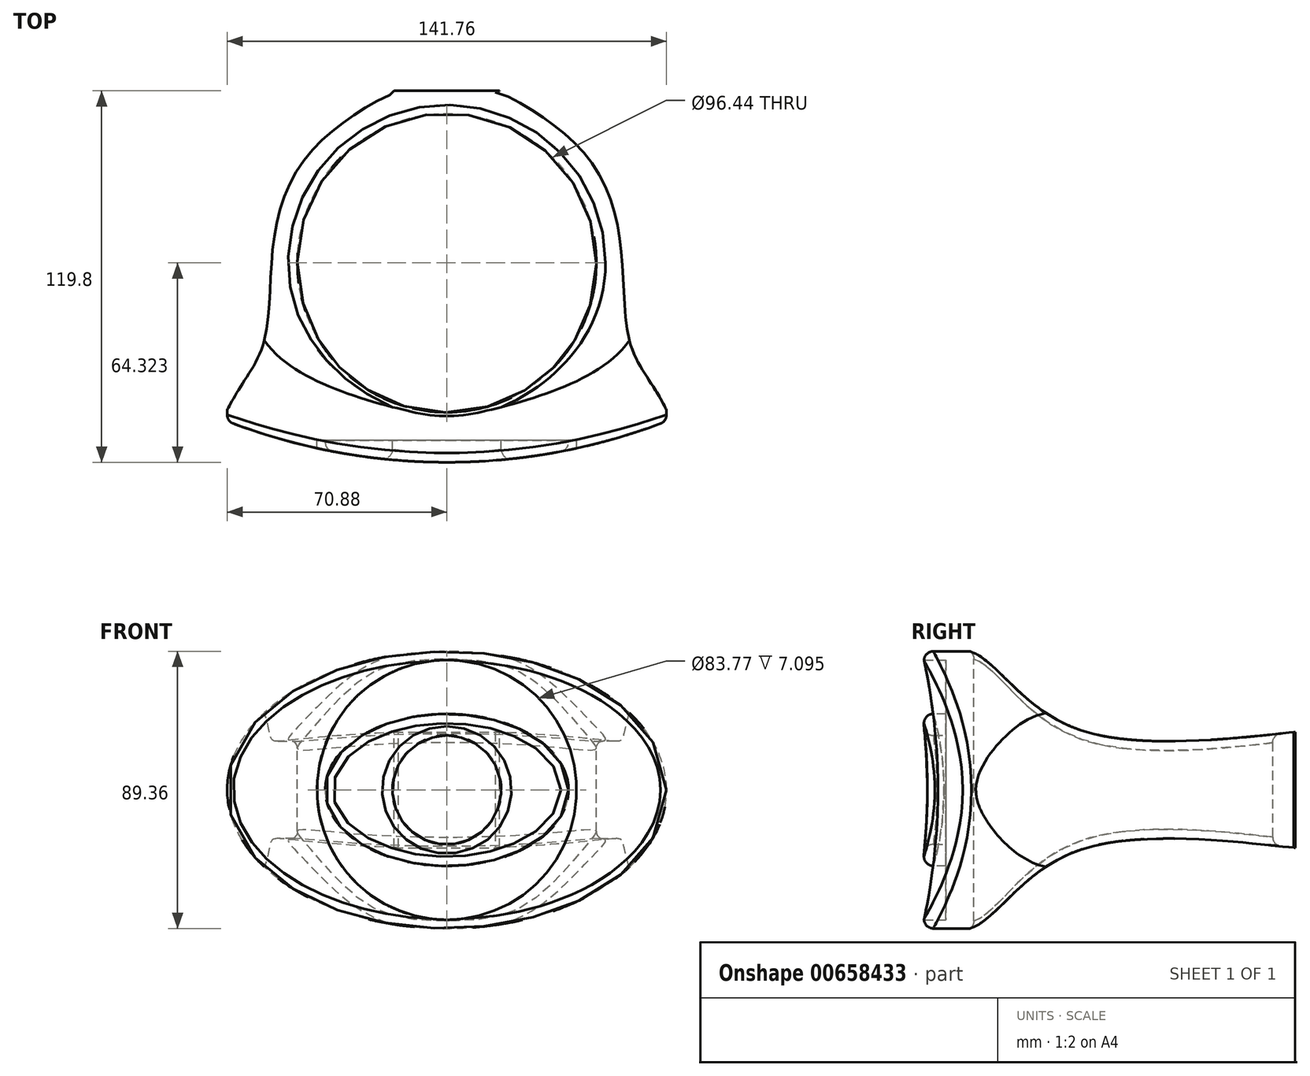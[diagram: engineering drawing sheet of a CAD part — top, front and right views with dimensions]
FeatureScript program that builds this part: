
annotation { "Feature Type Name" : "Feature", "Feature Type Description" : "" }
export const myFeature = defineFeature(function(context is Context, id is Id, definition is map)
    precondition{}
    {
        {
            var Q0;
            Q0=qCreatedBy(makeId("Front.planeOp"),FACE);
            var sketch = newSketch(context, id + "F0", { "sketchPlane" : qUnion([Q0])});
            skCircle(sketch, "E0", {"center": v(0, 0) * mm, "radius": 17.57 * mm});
            skCircle(sketch, "E1", {"center": v(0, 0) * mm, "radius": 41.88 * mm});
            skEllipse(sketch, "E2", {"center": v(0, 0) * mm, "majorRadius": 39.25 * mm, "minorRadius": 24.52 * mm, "majorAxis": v(1, 0)});
            skEllipse(sketch, "E3", {"center": v(0, 0) * mm, "majorRadius": 70.88 * mm, "minorRadius": 44.68 * mm, "majorAxis": v(1, 0)});
            skSolve(sketch);
        }
        {
            var Q0;
            Q0=makeQuery(id+"F0.imprint","IMPRINT",FACE,{"disambiguationData":[TD([[makeQuery(id+"F0.imprint","IMPRINT",EDGE,{"derivedFrom":sQuery(id+"F0.wireOp",EDGE,"E0")}),-1.0]])]});
            var Q1;
            Q1=makeQuery(id+"F0.imprint","IMPRINT",FACE,{"disambiguationData":[TD([[makeQuery(id+"F0.imprint","IMPRINT",EDGE,{"derivedFrom":sQuery(id+"F0.wireOp",EDGE,"E1")}),-1.0]])]});
            extrude(context, id + "F1", {"entities" : qUnion([Q0, Q1]), "depth" : 25.4 * mm, "offsetDistance" : 25.4 * mm});
        }
        {
            var Q0;
            Q0=qCreatedBy(makeId("Top.planeOp"),FACE);
            var sketch = newSketch(context, id + "F2", { "sketchPlane" : qUnion([Q0])});
            skCircle(sketch, "E4", {"center": v(0, 182.47) * mm, "radius": 196.57 * mm});
            skCircle(sketch, "E5", {"center": v(0, 182.47) * mm, "radius": 224.82 * mm});
            skSolve(sketch);
        }
        {
            var Q0;
            Q0=makeQuery(id+"F2.imprint","IMPRINT",FACE,{"disambiguationData":[TD([[makeQuery(id+"F2.imprint","IMPRINT",EDGE,{"derivedFrom":sQuery(id+"F2.wireOp",EDGE,"E4")}),-1.0]])]});
            extrude(context, id + "F3", {"entities" : qUnion([Q0]), "endBound" : BoundingType.SYMMETRIC, "depth" : 127 * mm, "offsetDistance" : 25.4 * mm});
        }
        {
            var Q0;
            Q0=makeQuery(id+"F3.opExtrude","SWEPT_BODY",BODY,{"disambiguationData":[OSD([sQuery(id+"F2.wireOp",EDGE,"E4"),sQuery(id+"F2.wireOp",EDGE,"E5")])]});
            var Q1;
            Q1=makeQuery(id+"F1.opExtrude","SWEPT_BODY",BODY,{"disambiguationData":[OSD([sQuery(id+"F0.wireOp",EDGE,"E1"),sQuery(id+"F0.wireOp",EDGE,"E3")])]});
            var Q2;
            Q2=makeQuery(id+"F1.opExtrude","SWEPT_BODY",BODY,{"disambiguationData":[OSD([sQuery(id+"F0.wireOp",EDGE,"E0"),sQuery(id+"F0.wireOp",EDGE,"E2")])]});
            booleanBodies(context, id + "F4", {"operationType" : BooleanOperationType.SUBTRACTION, "tools" : qUnion([Q0]), "targets" : qUnion([Q1, Q2])});
        }
        {
            var Q0;
            Q0=makeQuery(id+"F1.opExtrude","CAP_FACE",FACE,{"disambiguationData":[OSD([sQuery(id+"F0.wireOp",EDGE,"E1"),sQuery(id+"F0.wireOp",EDGE,"E3")])],"isStart":true});
            var sketch = newSketch(context, id + "F5", { "sketchPlane" : qUnion([Q0])});
            skEllipse(sketch, "E6", {"center": v(0, 0) * mm, "majorRadius": 70.88 * mm, "minorRadius": 44.68 * mm, "majorAxis": v(1, 0)});
            skSolve(sketch);
        }
        {
            var Q0;
            Q0 = qSketchRegion(id + "F5", true);
            extrude(context, id + "F6", {"entities" : qUnion([Q0]), "depth" : 105.7 * mm, "offsetDistance" : 25 * mm});
        }
        {
            var Q0;
            Q0=makeQuery(id+"F1.opExtrude","SWEPT_BODY",BODY,{"disambiguationData":[OSD([sQuery(id+"F0.wireOp",EDGE,"E0"),sQuery(id+"F0.wireOp",EDGE,"E2")])]});
            var Q1;
            Q1=makeQuery(id+"F1.opExtrude","SWEPT_BODY",BODY,{"disambiguationData":[OSD([sQuery(id+"F0.wireOp",EDGE,"E1"),sQuery(id+"F0.wireOp",EDGE,"E3")])]});
            var Q2;
            Q2=makeQuery(id+"F6.opExtrude","SWEPT_BODY",BODY,{"disambiguationData":[OSD([sQuery(id+"F5.wireOp",EDGE,"E6")])]});
            booleanBodies(context, id + "F7", {"operationType" : BooleanOperationType.UNION, "tools" : qUnion([Q0, Q1, Q2])});
        }
        {
            var Q0;
            Q0=qCreatedBy(makeId("Top.planeOp"),FACE);
            var sketch = newSketch(context, id + "F8", { "sketchPlane" : qUnion([Q0])});
            skCircle(sketch, "E7", {"center": v(0, 50.22) * mm, "radius": 48.22 * mm});
            skSolve(sketch);
        }
        {
            var Q0;
            Q0 = qSketchRegion(id + "F8", true);
            extrude(context, id + "F9", {"entities" : qUnion([Q0]), "operationType" : NewBodyOperationType.REMOVE, "endBound" : BoundingType.SYMMETRIC, "oppositeDirection" : true, "depth" : 100 * mm, "offsetDistance" : 25 * mm});
        }
        {
            var Q0;
            Q0=qCreatedBy(makeId("Top.planeOp"),FACE);
            var sketch = newSketch(context, id + "F10", { "sketchPlane" : qUnion([Q0])});
            skFitSpline(sketch, "E8", {"points": [v(-73.16, -11.53) * mm, v(-72.85, -3.9) * mm, v(-66.49, 10.46) * mm, v(-58.83, 25.54) * mm, v(-55.73, 58.48) * mm, v(-40.14, 89.97) * mm, v(-15.99, 105.25) * mm, v(-15.68, 105.25) * mm, v(-89.05, 104.33) * mm, v(-82.63, -12.15) * mm, v(-73.16, -11.53) * mm]});
            skFitSpline(sketch, "E9.MirrorC", {"points": [v(73.16, -11.53) * mm, v(72.85, -3.9) * mm, v(66.49, 10.46) * mm, v(58.83, 25.54) * mm, v(55.73, 58.48) * mm, v(40.14, 89.97) * mm, v(15.99, 105.25) * mm, v(15.68, 105.25) * mm, v(89.05, 104.33) * mm, v(82.63, -12.15) * mm, v(73.16, -11.53) * mm]});
            skSolve(sketch);
        }
        {
            var Q0;
            Q0 = qSketchRegion(id + "F10", true);
            extrude(context, id + "F11", {"entities" : qUnion([Q0]), "operationType" : NewBodyOperationType.REMOVE, "endBound" : BoundingType.SYMMETRIC, "oppositeDirection" : true, "depth" : 100 * mm, "offsetDistance" : 25 * mm});
        }
        {
            var Q0;
            Q0=qCreatedBy(makeId("Right.planeOp"),FACE);
            var sketch = newSketch(context, id + "F12", { "sketchPlane" : qUnion([Q0])});
            skFitSpline(sketch, "E10", {"points": [v(-21.85, 47.3) * mm, v(-14.13, 45.68) * mm, v(2.08, 44.23) * mm, v(38.16, 18.74) * mm, v(109.17, 18.74) * mm, v(109.96, 18.74) * mm, v(110.22, 55.95) * mm, v(-24.73, 63.03) * mm, v(-21.85, 47.3) * mm]});
            skFitSpline(sketch, "E11.MirrorC", {"points": [v(-21.85, -47.3) * mm, v(-14.13, -45.68) * mm, v(2.08, -44.23) * mm, v(38.16, -18.74) * mm, v(109.17, -18.74) * mm, v(109.96, -18.74) * mm, v(110.22, -55.95) * mm, v(-24.73, -63.03) * mm, v(-21.85, -47.3) * mm]});
            skSolve(sketch);
        }
        {
            var Q0;
            Q0=makeQuery(id+"F12.imprint","IMPRINT",FACE,{"disambiguationData":[TD([[makeQuery(id+"F12.imprint","IMPRINT",EDGE,{"derivedFrom":sQuery(id+"F12.wireOp",EDGE,"E10")}),1.0]])]});
            var Q1;
            Q1=makeQuery(id+"F12.imprint","IMPRINT",FACE,{"disambiguationData":[TD([[makeQuery(id+"F12.imprint","IMPRINT",EDGE,{"derivedFrom":sQuery(id+"F12.wireOp",EDGE,"E11.MirrorC")}),-1.0]])]});
            extrude(context, id + "F13", {"entities" : qUnion([Q0, Q1]), "operationType" : NewBodyOperationType.REMOVE, "endBound" : BoundingType.SYMMETRIC, "oppositeDirection" : true, "depth" : 150 * mm, "offsetDistance" : 25 * mm});
        }
        {
            var Q0;
            Q0=makeQuery(id+"F13.boolean.opBoolean","INTERSECT",EDGE,{"derivedFrom":[makeQuery(id+"F9.boolean.opBoolean","COPY",FACE,{"derivedFrom":makeQuery(id+"F9.opExtrude","SWEPT_FACE",FACE,{"disambiguationData":[OSD([sQuery(id+"F8.wireOp",EDGE,"E7")])]})}),makeQuery(id+"F13.opExtrude","SWEPT_FACE",FACE,{"disambiguationData":[OSD([sQuery(id+"F12.wireOp",EDGE,"E11.MirrorC")])]})]});
            var Q1;
            Q1=makeQuery(id+"F13.boolean.opBoolean","INTERSECT",EDGE,{"derivedFrom":[makeQuery(id+"F9.boolean.opBoolean","COPY",FACE,{"derivedFrom":makeQuery(id+"F9.opExtrude","SWEPT_FACE",FACE,{"disambiguationData":[OSD([sQuery(id+"F8.wireOp",EDGE,"E7")])]})}),makeQuery(id+"F13.opExtrude","SWEPT_FACE",FACE,{"disambiguationData":[OSD([sQuery(id+"F12.wireOp",EDGE,"E10")])]})]});
            var Q2;
            Q2=makeQuery(id+"F4.opBoolean","INTERSECT",EDGE,{"derivedFrom":[makeQuery(id+"F1.opExtrude","SWEPT_FACE",FACE,{"disambiguationData":[OSD([sQuery(id+"F0.wireOp",EDGE,"E3")])]}),makeQuery(id+"F3.opExtrude","SWEPT_FACE",FACE,{"disambiguationData":[OSD([sQuery(id+"F2.wireOp",EDGE,"E4")])]})]});
            var Q3;
            Q3=makeQuery(id+"F4.opBoolean","INTERSECT",EDGE,{"derivedFrom":[makeQuery(id+"F1.opExtrude","SWEPT_FACE",FACE,{"disambiguationData":[OSD([sQuery(id+"F0.wireOp",EDGE,"E2")])]}),makeQuery(id+"F3.opExtrude","SWEPT_FACE",FACE,{"disambiguationData":[OSD([sQuery(id+"F2.wireOp",EDGE,"E4")])]})]});
            var Q4;
            Q4=makeQuery(id+"F4.opBoolean","INTERSECT",EDGE,{"derivedFrom":[makeQuery(id+"F1.opExtrude","SWEPT_FACE",FACE,{"disambiguationData":[OSD([sQuery(id+"F0.wireOp",EDGE,"E0")])]}),makeQuery(id+"F3.opExtrude","SWEPT_FACE",FACE,{"disambiguationData":[OSD([sQuery(id+"F2.wireOp",EDGE,"E4")])]})]});
            fillet(context, id + "F14", {"entities" : qUnion([Q0, Q1, Q2, Q3, Q4]), "radius" : 3 * mm, "tangentPropagation" : true, "allowEdgeOverflow" : false});
        }
        {
            var Q0;
            Q0=makeQuery(id+"F7.opBoolean","SPLIT",FACE,{"disambiguationData":[TD([makeQuery(id+"F1.opExtrude","SWEPT_FACE",FACE,{"disambiguationData":[OSD([sQuery(id+"F0.wireOp",EDGE,"E1")])]})])],"derivedFrom":makeQuery(id+"F6.opExtrude","CAP_FACE",FACE,{"disambiguationData":[OSD([sQuery(id+"F5.wireOp",EDGE,"E6")])],"isStart":true})});
            var Q1;
            Q1=makeQuery(id+"F7.opBoolean","SPLIT",FACE,{"disambiguationData":[TD([makeQuery(id+"F1.opExtrude","SWEPT_FACE",FACE,{"disambiguationData":[OSD([sQuery(id+"F0.wireOp",EDGE,"E0")])]})])],"derivedFrom":makeQuery(id+"F6.opExtrude","CAP_FACE",FACE,{"disambiguationData":[OSD([sQuery(id+"F5.wireOp",EDGE,"E6")])],"isStart":true})});
            extrude(context, id + "F15", {"entities" : qUnion([Q0, Q1]), "operationType" : NewBodyOperationType.ADD, "depth" : 7 * mm, "offsetDistance" : 25 * mm});
        }
    });
